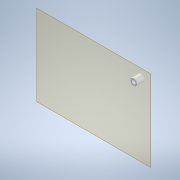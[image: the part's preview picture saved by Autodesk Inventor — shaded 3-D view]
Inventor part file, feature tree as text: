
AUTODESK INVENTOR PART (.ipt)
format: ipt  version: 2020 (Build 240168000, 168)  size: 100,864 bytes
history: native  units: in
note: dims shown in document units (in); Inventor stores cm internally (conversion verified against a paired STEP export)
features: other x4, plane x1, extrude x1, sketch x1, reference x1
ambient origin geometry x8: Origin, YZ Plane, XZ Plane, XY Plane, X Axis, Y Axis, Z Axis, Center Point
bodies: Solid1 (feature_tree)
feature tree (8):
  plane  "Work Plane1"
  extrude  "Extrusion1"  Depth=0.24in
  sketch  "Sketch1"  dims[d0=0.24in d1=0.0in d2=0.05in]
  reference  "Reference1"
  other  "<userpath>\Documents\Inventor\Drone\3DPrint\OdroidAssembly.iam"
  other  "OdroidAssembly.iam"
  other  "Odroid-XU4 v1:1"
  other  "Assembly1"
